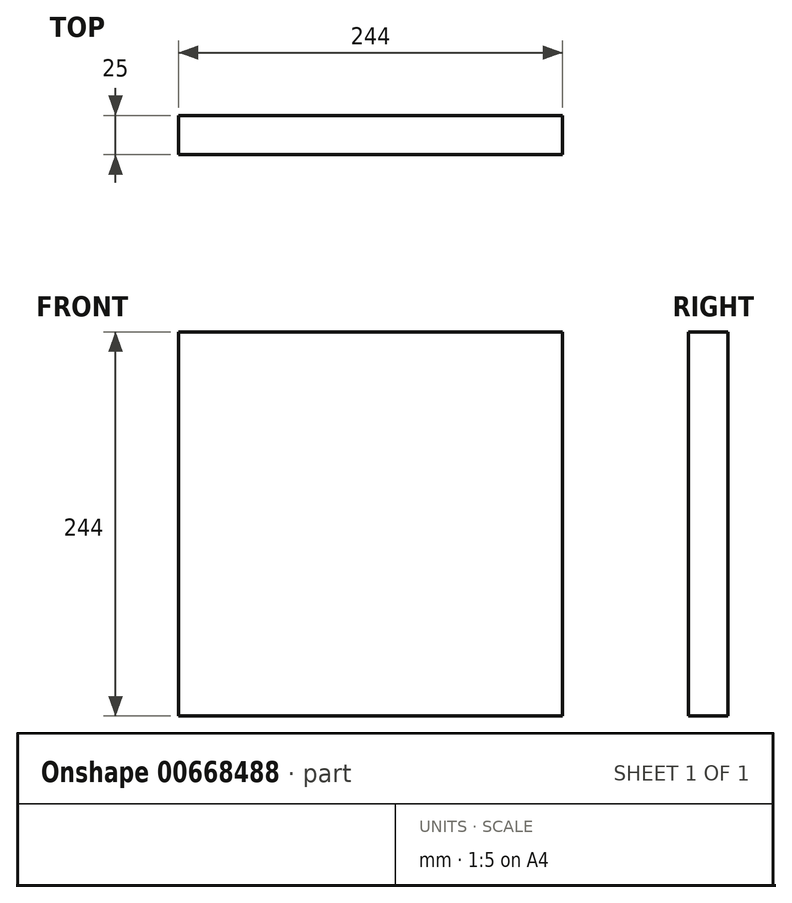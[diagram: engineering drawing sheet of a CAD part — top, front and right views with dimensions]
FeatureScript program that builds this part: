
annotation { "Feature Type Name" : "Feature", "Feature Type Description" : "" }
export const myFeature = defineFeature(function(context is Context, id is Id, definition is map)
    precondition{}
    {
        {
            var Q0;
            Q0=qCreatedBy(makeId("Front.planeOp"),FACE);
            var sketch = newSketch(context, id + "F0", { "sketchPlane" : qUnion([Q0])});
            skLineSegment(sketch, "E0.bottom", {"start": v(122, 122) * mm, "end": v(-122, 122) * mm});
            skLineSegment(sketch, "E0.top", {"start": v(122, -122) * mm, "end": v(-122, -122) * mm});
            skLineSegment(sketch, "E0.left", {"start": v(122, 122) * mm, "end": v(122, -122) * mm});
            skLineSegment(sketch, "E0.right", {"start": v(-122, 122) * mm, "end": v(-122, -122) * mm});
            skPoint(sketch, "E0.middle", {"position": v(0, 0) * mm});
            skSolve(sketch);
        }
        {
            var Q0;
            Q0=makeQuery(id+"F0.imprint","IMPRINT",FACE,{"disambiguationData":[TD([[makeQuery(id+"F0.imprint","IMPRINT",EDGE,{"derivedFrom":sQuery(id+"F0.wireOp",EDGE,"E0.bottom")}),1.0]])]});
            extrude(context, id + "F1", {"entities" : qUnion([Q0]), "depth" : 25 * mm, "offsetDistance" : 25 * mm});
        }
    });
